# Revit family: STE22
name_source: partatom
category: Lighting Fixtures
revit_build: Autodesk Revit Architecture 2012 (Build: 20110309_2315(x64)
units: mm (PartAtom-declared; Revit-internal decimal feet)

## types (8) — shared parameters
Backbox = White
Color Filter = 16777215
Default Elevation = 48.000"
Description = 2' × 2' Stratus® Recessed Indirect / 2 or 3-Lamp TT
Dimming Lamp Color Temperature Shift = <None>
Emit from Line Length = 23.000"
Glass = Glass
Lamp = 3
Manufacturer = Columbia Lighting
Manufacturer Fax = 866.898.1065
Model = STE22
Product Documentation Link = http://www.columbialighting.com
Product Page URL = http://www.columbialighting.com
Tilt Angle = -90.00°
URL = http://www.columbialighting.com
Wattage Comments = 42W

## per-type parameters (varying)
| type | Photometric Web File |
| STE22-214G-MPO | 3506.IES |
| STE22-217G-MPO-EU | 3490.IES |
| STE22-224G-MPO-EPU | 3503.IES |
| STE22-240TTG-MPO-EU | 3693.IES |
| STE22-314G-MPO-EPU | 3512.IES |
| STE22-324G-MPO-EPU | 3509.IES |
| STE22-317G-MPO-3EU | 3485.IES |
| STE22-317G-WPBMPO-3EU | 3486.IES |

## geometry (parser evidence)
native form markers: Blend x1, Sweep x1
no freeform markers — native parametric forms only
